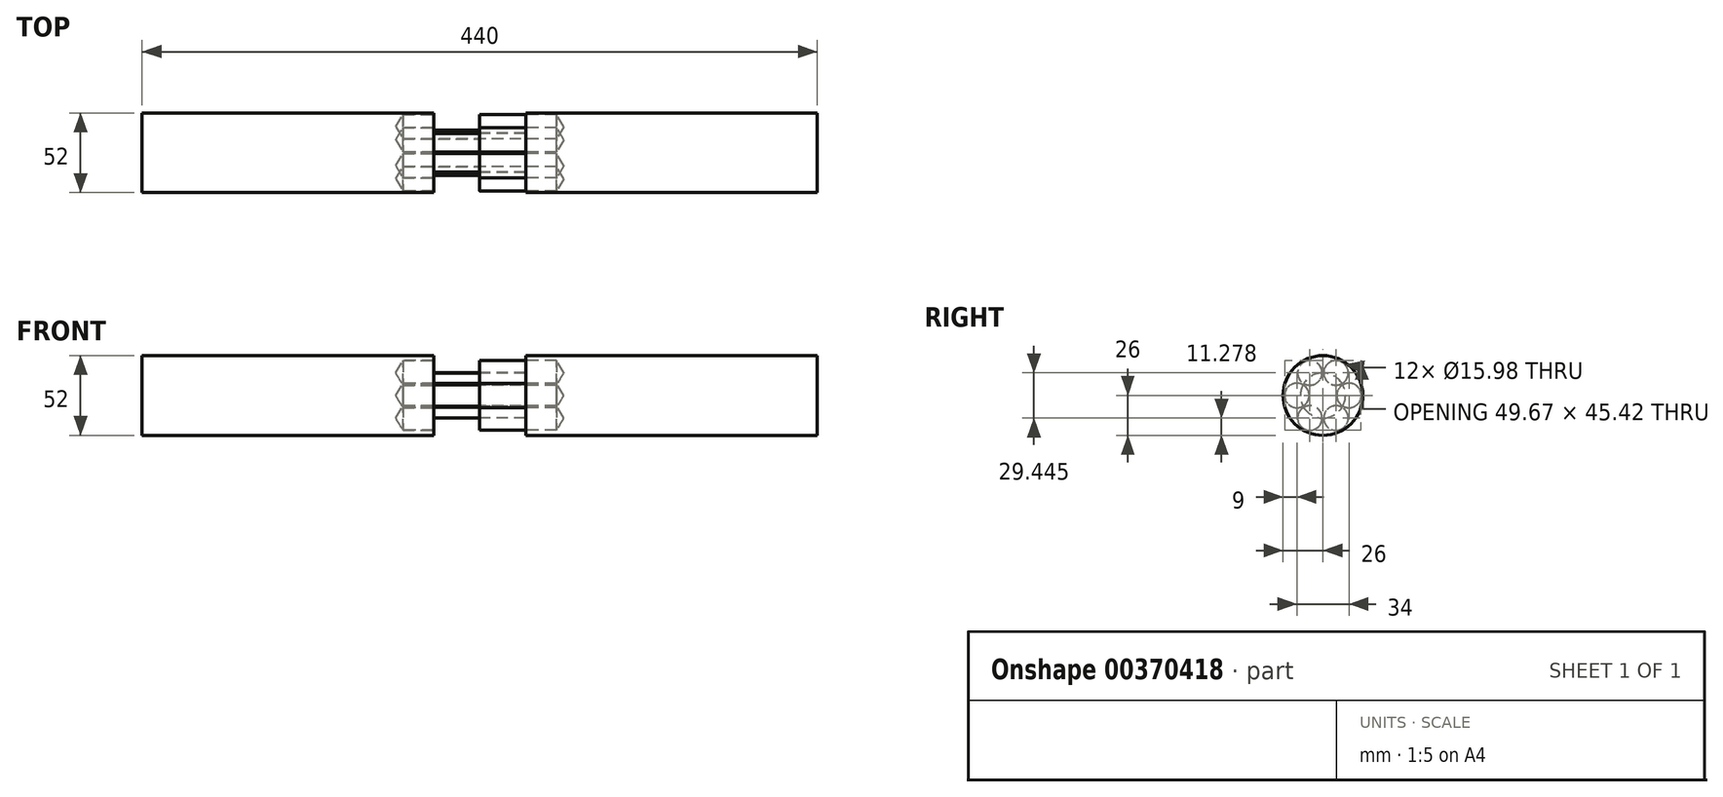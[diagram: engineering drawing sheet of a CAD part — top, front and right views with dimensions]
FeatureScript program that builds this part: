
annotation { "Feature Type Name" : "Feature", "Feature Type Description" : "" }
export const myFeature = defineFeature(function(context is Context, id is Id, definition is map)
    precondition{}
    {
        {
            var Q0;
            Q0=qCreatedBy(makeId("Right.planeOp"),FACE);
            var sketch = newSketch(context, id + "F0", { "sketchPlane" : qUnion([Q0])});
            skCircle(sketch, "E0", {"center": v(0, 0) * mm, "radius": 26 * mm});
            skSolve(sketch);
        }
        {
            var Q0;
            Q0=makeQuery(id+"F0.imprint","IMPRINT",FACE,{"disambiguationData":[TD([[makeQuery(id+"F0.imprint","IMPRINT",EDGE,{"derivedFrom":sQuery(id+"F0.wireOp",EDGE,"E0")}),1.0]])]});
            extrude(context, id + "F1", {"entities" : qUnion([Q0]), "oppositeDirection" : true, "depth" : 220 * mm, "offsetDistance" : 25 * mm});
        }
        {
            var Q0;
            Q0=qCreatedBy(makeId("Right.planeOp"),FACE);
            var sketch = newSketch(context, id + "F2", { "sketchPlane" : qUnion([Q0])});
            skCircle(sketch, "E1", {"center": v(0, 0) * mm, "radius": 26 * mm, "construction": true});
            skLineSegment(sketch, "E2", {"start": v(0, 0) * mm, "end": v(13, -22.52) * mm, "construction": true});
            skCircle(sketch, "E3", {"center": v(8.5, -14.72) * mm, "radius": 8 * mm});
            skLineSegment(sketch, "E4", {"start": v(0, 0) * mm, "end": v(0, -26) * mm, "construction": true});
            skSolve(sketch);
        }
        {
            var Q0;
            Q0=makeQuery(id+"F2.imprint","IMPRINT",FACE,{"disambiguationData":[TD([[makeQuery(id+"F2.imprint","IMPRINT",EDGE,{"derivedFrom":sQuery(id+"F2.wireOp",EDGE,"E3")}),1.0]])]});
            extrude(context, id + "F3", {"entities" : qUnion([Q0]), "depth" : 100 * mm, "offsetDistance" : 25 * mm, "symmetric" : true});
        }
        {
            var Q0;
            Q0=makeQuery(id+"F3.opExtrude","SWEPT_BODY",BODY,{"disambiguationData":[OSD([sQuery(id+"F2.wireOp",EDGE,"E3")])]});
            var Q1;
            Q1=makeQuery(id+"F1.opExtrude","SWEPT_FACE",FACE,{"disambiguationData":[OSD([sQuery(id+"F0.wireOp",EDGE,"E0")])]});
            circularPattern(context, id + "F4", {"entities" : qUnion([Q0]), "axis" : qUnion([Q1]), "angle" : 360 * degree, "instanceCount" : 6, "equalSpace" : true});
        }
        {
            var Q0;
            Q0=qCreatedBy(makeId("Right.planeOp"),FACE);
            var sketch = newSketch(context, id + "F5", { "sketchPlane" : qUnion([Q0])});
            skCircle(sketch, "E5", {"center": v(0, 0) * mm, "radius": 26 * mm});
            skCircle(sketch, "E6", {"center": v(-8.5, 14.72) * mm, "radius": 8 * mm, "construction": true});
            skCircle(sketch, "E7", {"center": v(8.5, 14.72) * mm, "radius": 8 * mm, "construction": true});
            skCircle(sketch, "E8", {"center": v(17, 0) * mm, "radius": 8 * mm, "construction": true});
            skCircle(sketch, "E9", {"center": v(8.5, -14.72) * mm, "radius": 8 * mm, "construction": true});
            skCircle(sketch, "E10", {"center": v(-8.5, -14.72) * mm, "radius": 8 * mm, "construction": true});
            skCircle(sketch, "E11", {"center": v(-17, 0) * mm, "radius": 8 * mm, "construction": true});
            skCircle(sketch, "E12", {"center": v(0, 0) * mm, "radius": 14.72 * mm});
            skLineSegment(sketch, "E13", {"start": v(-8.5, 14.72) * mm, "end": v(-17, 0) * mm, "construction": true});
            skSolve(sketch);
        }
        {
            var Q0;
            Q0=sQuery(id+"F5.wireOp",VERTEX,"E6.center");
            var Q1;
            Q1=sQuery(id+"F5.wireOp",VERTEX,"E7.center");
            var Q2;
            Q2=sQuery(id+"F5.wireOp",VERTEX,"E11.center");
            var Q3;
            Q3=sQuery(id+"F5.wireOp",VERTEX,"E10.center");
            var Q4;
            Q4=sQuery(id+"F5.wireOp",VERTEX,"E9.center");
            var Q5;
            Q5=sQuery(id+"F5.wireOp",VERTEX,"E8.center");
            var Q6;
            Q6=makeQuery(id+"F1.opExtrude","SWEPT_BODY",BODY,{"disambiguationData":[OSD([sQuery(id+"F0.wireOp",EDGE,"E0")])]});
            hole(context, id + "F6", {"style" : HoleStyle.SIMPLE, "endStyle" : HoleEndStyle.BLIND, "holeDiameter" : 15.98 * mm, "majorDiameter" : 5 * mm, "holeDepth" : 50 * mm, "isTappedThrough" : true, "tappedDepth" : 20 * mm, "tapClearance" : 3, "locations" : qUnion([Q0, Q1, Q2, Q3, Q4, Q5]), "scope" : qUnion([Q6])});
        }
        {
            var Q0;
            Q0=makeQuery(id+"F5.imprint","IMPRINT",FACE,{"disambiguationData":[TD([[makeQuery(id+"F5.imprint","IMPRINT",EDGE,{"derivedFrom":sQuery(id+"F5.wireOp",EDGE,"E5")}),1.0]])]});
            extrude(context, id + "F7", {"entities" : qUnion([Q0]), "operationType" : NewBodyOperationType.REMOVE, "oppositeDirection" : true, "depth" : 30 * mm, "offsetDistance" : 25 * mm});
        }
        {
            var Q0;
            Q0=makeQuery(id+"F1.opExtrude","SWEPT_BODY",BODY,{"disambiguationData":[OSD([sQuery(id+"F0.wireOp",EDGE,"E0")])]});
            var Q1;
            Q1=qCreatedBy(makeId("Right.planeOp"),FACE);
            mirror(context, id + "F8", {"entities" : qUnion([Q0]), "mirrorPlane" : qUnion([Q1])});
        }
    });
